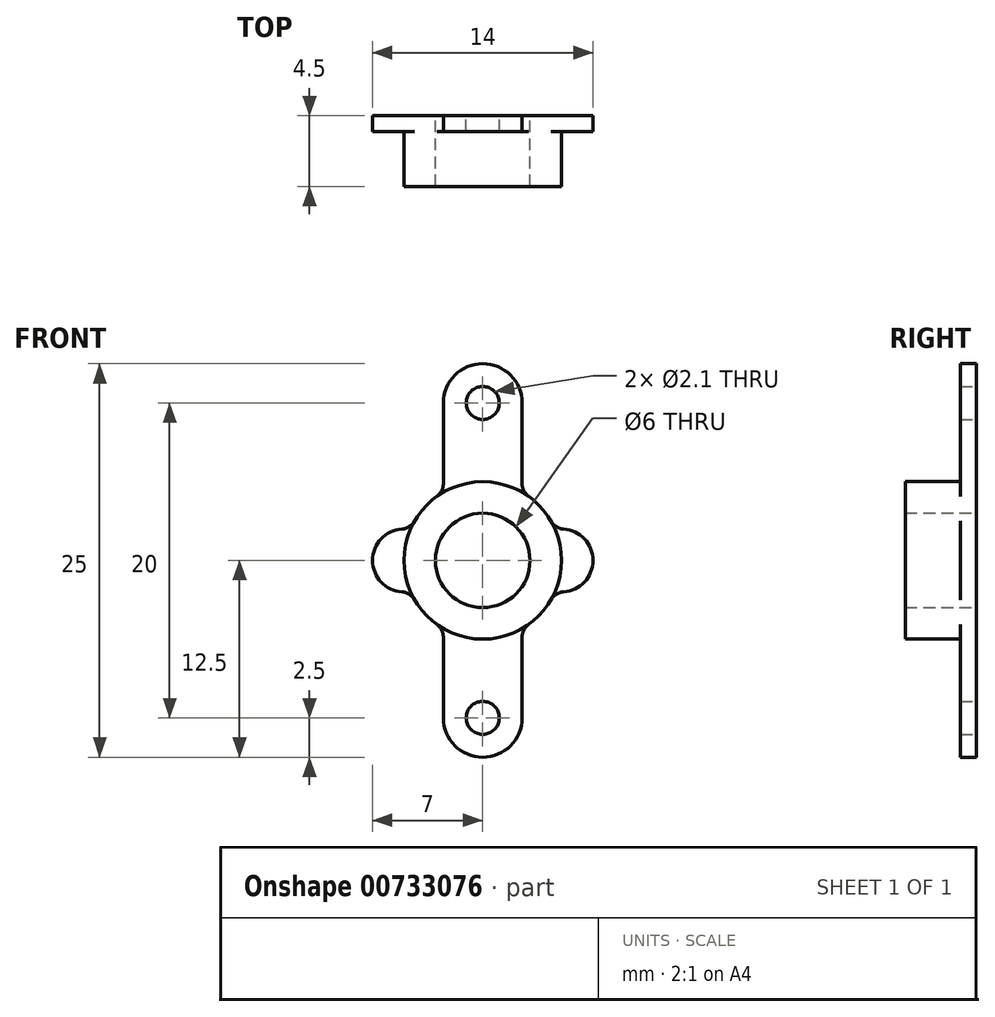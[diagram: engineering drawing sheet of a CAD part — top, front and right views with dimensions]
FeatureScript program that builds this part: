
annotation { "Feature Type Name" : "Feature", "Feature Type Description" : "" }
export const myFeature = defineFeature(function(context is Context, id is Id, definition is map)
    precondition{}
    {
        {
            var Q0;
            Q0=qCreatedBy(makeId("Right.planeOp"),FACE);
            var sketch = newSketch(context, id + "F0", { "sketchPlane" : qUnion([Q0])});
            skLineSegment(sketch, "E0.bottom", {"start": v(0, 0) * mm, "end": v(-4.5, 0) * mm});
            skLineSegment(sketch, "E0.top", {"start": v(0, 5) * mm, "end": v(-4.5, 5) * mm});
            skLineSegment(sketch, "E0.left", {"start": v(0, 0) * mm, "end": v(0, 5) * mm});
            skLineSegment(sketch, "E0.right", {"start": v(-4.5, 0) * mm, "end": v(-4.5, 5) * mm});
            skSolve(sketch);
        }
        {
            var Q0;
            Q0 = qSketchRegion(id + "F0", true);
            var Q1;
            Q1=sQuery(id+"F0.wireOp",EDGE,"E0.bottom");
            revolve(context, id + "F1", {"surfaceOperationType" : NewSurfaceOperationType.NEW, "entities" : qUnion([Q0]), "axis" : qUnion([Q1]), "revolveType" : RevolveType.FULL});
        }
        {
            var Q0;
            Q0=makeQuery(id+"F1.opRevolve","SWEPT_FACE",FACE,{"disambiguationData":[OSD([sQuery(id+"F0.wireOp",EDGE,"E0.left")])]});
            var sketch = newSketch(context, id + "F2", { "sketchPlane" : qUnion([Q0])});
            skLineSegment(sketch, "E1.bottom", {"start": v(2.5, -10) * mm, "end": v(-2.5, -10) * mm});
            skLineSegment(sketch, "E1.top", {"start": v(2.5, 10) * mm, "end": v(-2.5, 10) * mm});
            skLineSegment(sketch, "E1.left", {"start": v(2.5, -10) * mm, "end": v(2.5, 10) * mm});
            skLineSegment(sketch, "E1.right", {"start": v(-2.5, -10) * mm, "end": v(-2.5, 10) * mm});
            skPoint(sketch, "E1.middle", {"position": v(0, 0) * mm});
            skArc(sketch, "E2", {"start": v(-2.5, 10) * mm, "mid": v(0, 12.5) * mm, "end": v(2.5, 10) * mm});
            skArc(sketch, "E3", {"start": v(-2.5, -10) * mm, "mid": v(0, -12.5) * mm, "end": v(2.5, -10) * mm});
            skCircle(sketch, "E4", {"center": v(0, 10) * mm, "radius": 1.05 * mm});
            skCircle(sketch, "E5", {"center": v(0, -10) * mm, "radius": 1.05 * mm});
            skSolve(sketch);
        }
        {
            var Q0;
            Q0 = qSketchRegion(id + "F2", true);
            extrude(context, id + "F3", {"entities" : qUnion([Q0]), "operationType" : NewBodyOperationType.ADD, "oppositeDirection" : true, "depth" : 1 * mm, "offsetDistance" : 25 * mm});
        }
        {
            var Q0;
            Q0=makeQuery(id+"F3.boolean.opBoolean","MERGE",FACE,{"derivedFrom":[makeQuery(id+"F1.opRevolve","SWEPT_FACE",FACE,{"disambiguationData":[OSD([sQuery(id+"F0.wireOp",EDGE,"E0.left")])]}),makeQuery(id+"F3.opExtrude","CAP_FACE",FACE,{"disambiguationData":[OSD([sQuery(id+"F2.wireOp",EDGE,"E1.left"),sQuery(id+"F2.wireOp",EDGE,"E1.right"),sQuery(id+"F2.wireOp",EDGE,"E2"),sQuery(id+"F2.wireOp",EDGE,"E3"),sQuery(id+"F2.wireOp",EDGE,"E4"),sQuery(id+"F2.wireOp",EDGE,"E5")])],"isStart":true})]});
            var sketch = newSketch(context, id + "F4", { "sketchPlane" : qUnion([Q0])});
            skLineSegment(sketch, "E6.bottom", {"start": v(5, -2) * mm, "end": v(-5, -2) * mm});
            skLineSegment(sketch, "E6.top", {"start": v(5, 2) * mm, "end": v(-5, 2) * mm});
            skLineSegment(sketch, "E6.left", {"start": v(5, -2) * mm, "end": v(5, 2) * mm});
            skLineSegment(sketch, "E6.right", {"start": v(-5, -2) * mm, "end": v(-5, 2) * mm});
            skPoint(sketch, "E6.middle", {"position": v(0, 0) * mm});
            skArc(sketch, "E7", {"start": v(-5, 2) * mm, "mid": v(-7, 0) * mm, "end": v(-5, -2) * mm});
            skArc(sketch, "E8", {"start": v(5, 2) * mm, "mid": v(7, 0) * mm, "end": v(5, -2) * mm});
            skSolve(sketch);
        }
        {
            var Q0;
            Q0 = qSketchRegion(id + "F4", true);
            extrude(context, id + "F5", {"entities" : qUnion([Q0]), "operationType" : NewBodyOperationType.ADD, "oppositeDirection" : true, "depth" : 1 * mm, "offsetDistance" : 25 * mm});
        }
        {
            var Q0;
            Q0=makeQuery(id+"F3.boolean.opBoolean","INTERSECT",EDGE,{"disambiguationData":[OD(1.0)],"derivedFrom":[makeQuery(id+"F1.opRevolve","SWEPT_FACE",FACE,{"disambiguationData":[OSD([sQuery(id+"F0.wireOp",EDGE,"E0.top")])]}),makeQuery(id+"F3.opExtrude","SWEPT_FACE",FACE,{"disambiguationData":[OSD([sQuery(id+"F2.wireOp",EDGE,"E1.left")])]})]});
            var Q1;
            Q1=makeQuery(id+"F5.boolean.opBoolean","INTERSECT",EDGE,{"disambiguationData":[OD(0.0)],"derivedFrom":[makeQuery(id+"F1.opRevolve","SWEPT_FACE",FACE,{"disambiguationData":[OSD([sQuery(id+"F0.wireOp",EDGE,"E0.top")])]}),makeQuery(id+"F5.opExtrude","SWEPT_FACE",FACE,{"disambiguationData":[OSD([sQuery(id+"F4.wireOp",EDGE,"E6.top")])]})]});
            var Q2;
            Q2=makeQuery(id+"F5.boolean.opBoolean","INTERSECT",EDGE,{"disambiguationData":[OD(0.0)],"derivedFrom":[makeQuery(id+"F1.opRevolve","SWEPT_FACE",FACE,{"disambiguationData":[OSD([sQuery(id+"F0.wireOp",EDGE,"E0.top")])]}),makeQuery(id+"F5.opExtrude","SWEPT_FACE",FACE,{"disambiguationData":[OSD([sQuery(id+"F4.wireOp",EDGE,"E6.bottom")])]})]});
            var Q3;
            Q3=makeQuery(id+"F3.boolean.opBoolean","INTERSECT",EDGE,{"disambiguationData":[OD(0.0)],"derivedFrom":[makeQuery(id+"F1.opRevolve","SWEPT_FACE",FACE,{"disambiguationData":[OSD([sQuery(id+"F0.wireOp",EDGE,"E0.top")])]}),makeQuery(id+"F3.opExtrude","SWEPT_FACE",FACE,{"disambiguationData":[OSD([sQuery(id+"F2.wireOp",EDGE,"E1.left")])]})]});
            var Q4;
            Q4=makeQuery(id+"F3.boolean.opBoolean","INTERSECT",EDGE,{"disambiguationData":[OD(0.0)],"derivedFrom":[makeQuery(id+"F1.opRevolve","SWEPT_FACE",FACE,{"disambiguationData":[OSD([sQuery(id+"F0.wireOp",EDGE,"E0.top")])]}),makeQuery(id+"F3.opExtrude","SWEPT_FACE",FACE,{"disambiguationData":[OSD([sQuery(id+"F2.wireOp",EDGE,"E1.right")])]})]});
            var Q5;
            Q5=makeQuery(id+"F5.boolean.opBoolean","INTERSECT",EDGE,{"disambiguationData":[OD(1.0)],"derivedFrom":[makeQuery(id+"F1.opRevolve","SWEPT_FACE",FACE,{"disambiguationData":[OSD([sQuery(id+"F0.wireOp",EDGE,"E0.top")])]}),makeQuery(id+"F5.opExtrude","SWEPT_FACE",FACE,{"disambiguationData":[OSD([sQuery(id+"F4.wireOp",EDGE,"E6.bottom")])]})]});
            var Q6;
            Q6=makeQuery(id+"F3.boolean.opBoolean","INTERSECT",EDGE,{"disambiguationData":[OD(1.0)],"derivedFrom":[makeQuery(id+"F1.opRevolve","SWEPT_FACE",FACE,{"disambiguationData":[OSD([sQuery(id+"F0.wireOp",EDGE,"E0.top")])]}),makeQuery(id+"F3.opExtrude","SWEPT_FACE",FACE,{"disambiguationData":[OSD([sQuery(id+"F2.wireOp",EDGE,"E1.right")])]})]});
            var Q7;
            Q7=makeQuery(id+"F5.boolean.opBoolean","INTERSECT",EDGE,{"disambiguationData":[OD(1.0)],"derivedFrom":[makeQuery(id+"F1.opRevolve","SWEPT_FACE",FACE,{"disambiguationData":[OSD([sQuery(id+"F0.wireOp",EDGE,"E0.top")])]}),makeQuery(id+"F5.opExtrude","SWEPT_FACE",FACE,{"disambiguationData":[OSD([sQuery(id+"F4.wireOp",EDGE,"E6.top")])]})]});
            fillet(context, id + "F6", {"entities" : qUnion([Q0, Q1, Q2, Q3, Q4, Q5, Q6, Q7]), "radius" : 1 * mm, "tangentPropagation" : true, "allowEdgeOverflow" : false});
        }
        {
            var Q0;
            Q0=makeQuery(id+"F5.boolean.opBoolean","MERGE",FACE,{"derivedFrom":[makeQuery(id+"F3.boolean.opBoolean","MERGE",FACE,{"derivedFrom":[makeQuery(id+"F1.opRevolve","SWEPT_FACE",FACE,{"disambiguationData":[OSD([sQuery(id+"F0.wireOp",EDGE,"E0.left")])]}),makeQuery(id+"F3.opExtrude","CAP_FACE",FACE,{"disambiguationData":[OSD([sQuery(id+"F2.wireOp",EDGE,"E1.left"),sQuery(id+"F2.wireOp",EDGE,"E1.right"),sQuery(id+"F2.wireOp",EDGE,"E2"),sQuery(id+"F2.wireOp",EDGE,"E3"),sQuery(id+"F2.wireOp",EDGE,"E4"),sQuery(id+"F2.wireOp",EDGE,"E5")])],"isStart":true})]}),makeQuery(id+"F5.opExtrude","CAP_FACE",FACE,{"disambiguationData":[OSD([sQuery(id+"F4.wireOp",EDGE,"E6.bottom"),sQuery(id+"F4.wireOp",EDGE,"E6.top"),sQuery(id+"F4.wireOp",EDGE,"E7"),sQuery(id+"F4.wireOp",EDGE,"E8")])],"isStart":true})]});
            var sketch = newSketch(context, id + "F7", { "sketchPlane" : qUnion([Q0])});
            skCircle(sketch, "E9", {"center": v(0, 0) * mm, "radius": 3 * mm});
            skSolve(sketch);
        }
        {
            var Q0;
            Q0 = qSketchRegion(id + "F7", true);
            extrude(context, id + "F8", {"entities" : qUnion([Q0]), "operationType" : NewBodyOperationType.REMOVE, "endBound" : BoundingType.THROUGH_ALL, "oppositeDirection" : true, "depth" : 25 * mm, "offsetDistance" : 25 * mm});
        }
    });
